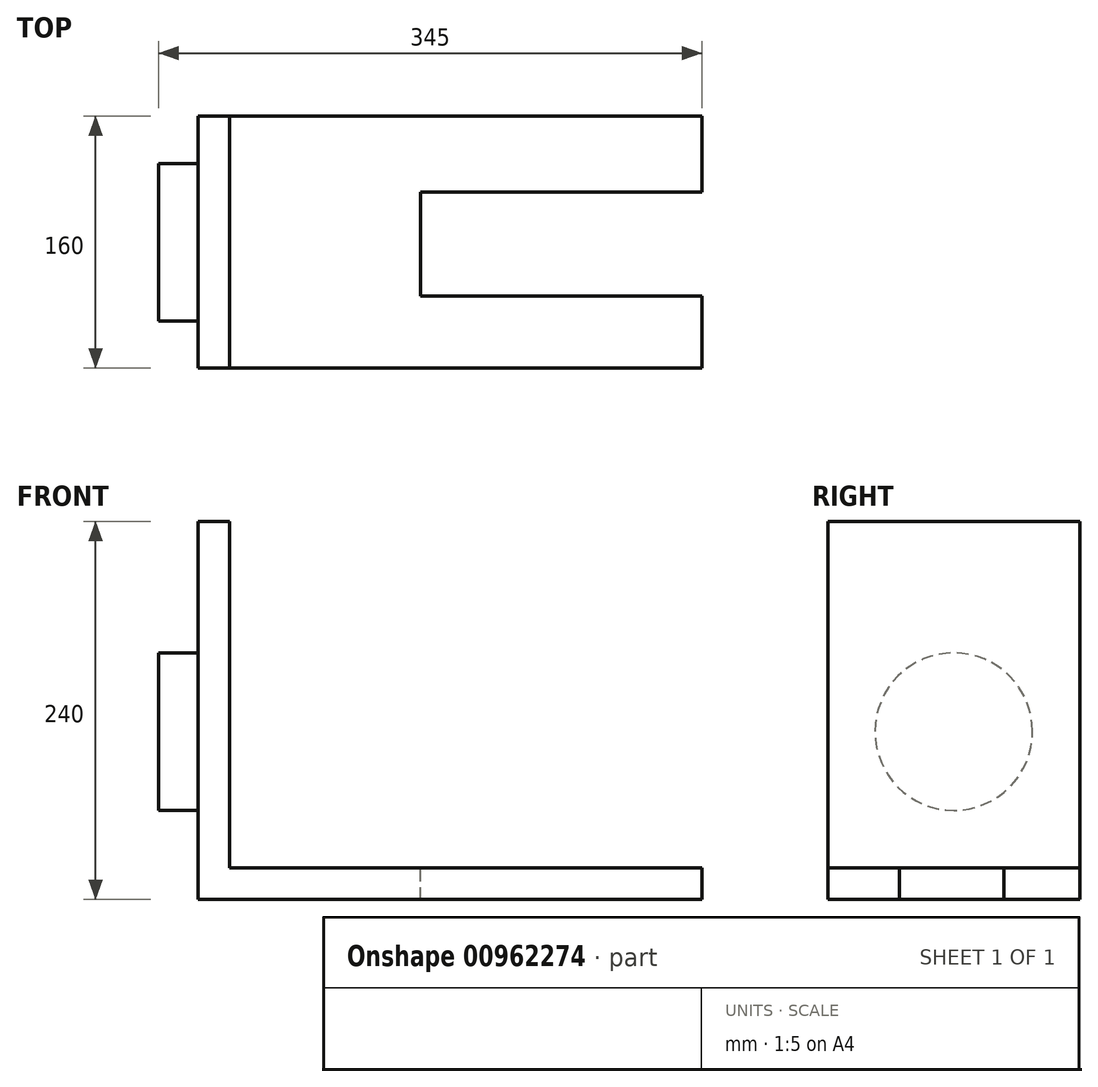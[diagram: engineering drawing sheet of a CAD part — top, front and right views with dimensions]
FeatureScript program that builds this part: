
annotation { "Feature Type Name" : "Feature", "Feature Type Description" : "" }
export const myFeature = defineFeature(function(context is Context, id is Id, definition is map)
    precondition{}
    {
        {
            var Q0;
            Q0=qCreatedBy(makeId("Front.planeOp"),FACE);
            var sketch = newSketch(context, id + "F0", { "sketchPlane" : qUnion([Q0])});
            skLineSegment(sketch, "E0", {"start": v(-151.93, 15.62) * mm, "end": v(-151.93, -106.56) * mm});
            skLineSegment(sketch, "E1", {"start": v(-151.93, -106.56) * mm, "end": v(168.07, -106.56) * mm});
            skLineSegment(sketch, "E2", {"start": v(168.07, -106.56) * mm, "end": v(168.07, -86.56) * mm});
            skLineSegment(sketch, "E3", {"start": v(168.07, -86.56) * mm, "end": v(-131.93, -86.56) * mm});
            skLineSegment(sketch, "E4", {"start": v(-131.93, -86.56) * mm, "end": v(-131.93, 133.44) * mm});
            skLineSegment(sketch, "E5", {"start": v(-151.93, 15.62) * mm, "end": v(-151.93, 133.44) * mm});
            skLineSegment(sketch, "E6", {"start": v(-151.93, 133.44) * mm, "end": v(-131.93, 133.44) * mm});
            skSolve(sketch);
        }
        {
            var Q0;
            Q0=makeQuery(id+"F0.imprint","IMPRINT",FACE,{"disambiguationData":[TD([[makeQuery(id+"F0.imprint","IMPRINT",EDGE,{"derivedFrom":sQuery(id+"F0.wireOp",EDGE,"E0")}),1.0]])]});
            extrude(context, id + "F1", {"entities" : qUnion([Q0]), "endBound" : BoundingType.SYMMETRIC, "depth" : 160 * mm, "offsetDistance" : 25 * mm});
        }
        {
            var Q0;
            Q0=makeQuery(id+"F1.opExtrude","SWEPT_FACE",FACE,{"disambiguationData":[OSD([sQuery(id+"F0.wireOp",EDGE,"E3")])]});
            var sketch = newSketch(context, id + "F2", { "sketchPlane" : qUnion([Q0])});
            skLineSegment(sketch, "E7.bottom", {"start": v(168.07, -34.4) * mm, "end": v(-10.68, -34.4) * mm});
            skLineSegment(sketch, "E7.top", {"start": v(168.07, 31.74) * mm, "end": v(-10.68, 31.74) * mm});
            skLineSegment(sketch, "E7.left", {"start": v(168.07, -34.4) * mm, "end": v(168.07, 31.74) * mm});
            skLineSegment(sketch, "E7.right", {"start": v(-10.68, -34.4) * mm, "end": v(-10.68, 31.74) * mm});
            skSolve(sketch);
        }
        {
            var Q0;
            Q0=makeQuery(id+"F2.imprint","IMPRINT",FACE,{"disambiguationData":[TD([[makeQuery(id+"F2.imprint","IMPRINT",EDGE,{"derivedFrom":sQuery(id+"F2.wireOp",EDGE,"E7.bottom")}),-1.0]])]});
            extrude(context, id + "F3", {"entities" : qUnion([Q0]), "operationType" : NewBodyOperationType.REMOVE, "oppositeDirection" : true, "depth" : 25 * mm, "offsetDistance" : 25 * mm});
        }
        {
            var Q0;
            Q0=makeQuery(id+"F1.opExtrude","SWEPT_FACE",FACE,{"disambiguationData":[OSD([sQuery(id+"F0.wireOp",EDGE,"E0"),sQuery(id+"F0.wireOp",EDGE,"E5")])]});
            var sketch = newSketch(context, id + "F4", { "sketchPlane" : qUnion([Q0])});
            skCircle(sketch, "E8", {"center": v(0, 0) * mm, "radius": 50 * mm});
            skSolve(sketch);
        }
        {
            var Q0;
            Q0=makeQuery(id+"F4.imprint","IMPRINT",FACE,{"disambiguationData":[TD([[makeQuery(id+"F4.imprint","IMPRINT",EDGE,{"derivedFrom":sQuery(id+"F4.wireOp",EDGE,"E8")}),1.0]])]});
            extrude(context, id + "F5", {"entities" : qUnion([Q0]), "operationType" : NewBodyOperationType.ADD, "depth" : 25 * mm, "offsetDistance" : 25 * mm});
        }
    });
